# Revit family: Landing Plate
name_source: partatom
category: Generic Models
units: mm (PartAtom-declared; Revit-internal decimal feet)

## family parameters
Always vertical = Yes
Can host rebar = No
Cut with Voids When Loaded = No
Maintain Annotation Orientation = No
Part Type = Normal
Room Calculation Point = No
Round Connector Dimension = Use Diameter
Shared = No
Work Plane-Based = No

## types (1)
- Landing Plate
    Comb Angle = 39.74°
    Comb Teeth Depth = 100 mm  [stored 0.328084 ft]
    Curved Length = 332 mm
    Default Elevation = 0 mm  [stored 0 ft]
    Extension beyond newel = 1500 mm  [stored 4.92126 ft]
    Landing Depth = 2552 mm
    Landing Plate Thickness = 120 mm
    Landing Plate Upper Length = 2220 mm
    Landing Plate Width = 2700 mm  [stored 8.85827 ft]
    Material = Stainless Steel
    Newel Width Left = 250 mm  [stored 0.82021 ft]
    Newel Width Right = 250 mm  [stored 0.82021 ft]
    Radius of Curvature = 519 mm

note: [stored X ft] marks values corroborated as IEEE doubles in the binary element streams (Revit-internal decimal feet)

## geometry (parser evidence)
native form markers: Sweep x1
no freeform markers — native parametric forms only
